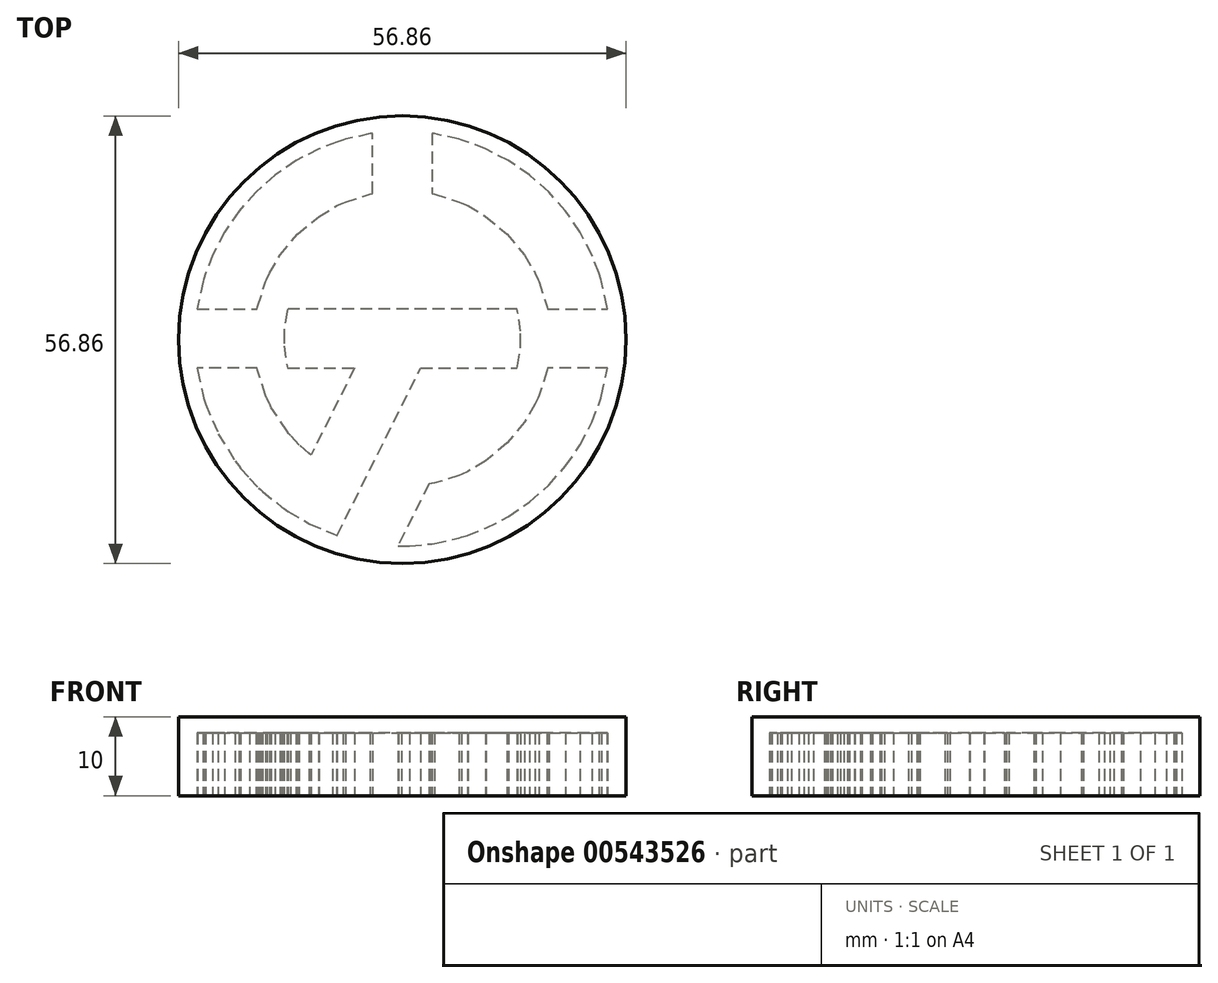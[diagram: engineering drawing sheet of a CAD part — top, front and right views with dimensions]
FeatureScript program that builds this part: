
annotation { "Feature Type Name" : "Feature", "Feature Type Description" : "" }
export const myFeature = defineFeature(function(context is Context, id is Id, definition is map)
    precondition{}
    {
        {
            var Q0;
            Q0=qCreatedBy(makeId("Top.planeOp"),FACE);
            var sketch = newSketch(context, id + "F0", { "sketchPlane" : qUnion([Q0])});
            skLineSegment(sketch, "E0", {"start": v(17.23, -7.39) * mm, "end": v(16.88, -8.2) * mm});
            skLineSegment(sketch, "E1", {"start": v(16.88, -8.2) * mm, "end": v(15.52, -10.46) * mm});
            skLineSegment(sketch, "E2", {"start": v(15.52, -10.46) * mm, "end": v(13.29, -13.15) * mm});
            skLineSegment(sketch, "E3", {"start": v(13.29, -13.15) * mm, "end": v(10.6, -15.39) * mm});
            skLineSegment(sketch, "E4", {"start": v(10.6, -15.39) * mm, "end": v(8.32, -16.75) * mm});
            skLineSegment(sketch, "E5", {"start": v(8.32, -16.75) * mm, "end": v(7.52, -17.1) * mm});
            skLineSegment(sketch, "E6", {"start": v(7.52, -17.1) * mm, "end": v(7.22, -17.23) * mm});
            skLineSegment(sketch, "E7", {"start": v(7.22, -17.23) * mm, "end": v(4.09, -18.23) * mm});
            skLineSegment(sketch, "E8", {"start": v(4.09, -18.23) * mm, "end": v(3.76, -18.3) * mm});
            skLineSegment(sketch, "E9", {"start": v(3.76, -18.3) * mm, "end": v(3.73, -18.3) * mm});
            skLineSegment(sketch, "E10", {"start": v(3.73, -18.3) * mm, "end": v(3.4, -18.36) * mm});
            skLineSegment(sketch, "E11", {"start": v(3.4, -18.36) * mm, "end": v(3.38, -18.36) * mm});
            skLineSegment(sketch, "E12", {"start": v(3.38, -18.36) * mm, "end": v(-0.54, -26.18) * mm});
            skLineSegment(sketch, "E13", {"start": v(-0.54, -26.18) * mm, "end": v(-0.5, -26.19) * mm});
            skLineSegment(sketch, "E14", {"start": v(-0.5, -26.19) * mm, "end": v(-0.12, -26.2) * mm});
            skLineSegment(sketch, "E15", {"start": v(-0.12, -26.2) * mm, "end": v(0, -26.2) * mm});
            skLineSegment(sketch, "E16", {"start": v(0, -26.2) * mm, "end": v(0.94, -26.2) * mm});
            skLineSegment(sketch, "E17", {"start": v(0.94, -26.2) * mm, "end": v(3.45, -25.97) * mm});
            skLineSegment(sketch, "E18", {"start": v(3.45, -25.97) * mm, "end": v(3.76, -25.92) * mm});
            skLineSegment(sketch, "E19", {"start": v(3.76, -25.92) * mm, "end": v(4.08, -25.88) * mm});
            skLineSegment(sketch, "E20", {"start": v(4.08, -25.88) * mm, "end": v(7.22, -25.18) * mm});
            skLineSegment(sketch, "E21", {"start": v(7.22, -25.18) * mm, "end": v(7.52, -25.09) * mm});
            skLineSegment(sketch, "E22", {"start": v(7.52, -25.09) * mm, "end": v(8.3, -24.85) * mm});
            skLineSegment(sketch, "E23", {"start": v(8.3, -24.85) * mm, "end": v(10.61, -23.95) * mm});
            skLineSegment(sketch, "E24", {"start": v(10.61, -23.95) * mm, "end": v(13.51, -22.45) * mm});
            skLineSegment(sketch, "E25", {"start": v(13.51, -22.45) * mm, "end": v(16.18, -20.61) * mm});
            skLineSegment(sketch, "E26", {"start": v(16.18, -20.61) * mm, "end": v(18.6, -18.47) * mm});
            skLineSegment(sketch, "E27", {"start": v(18.6, -18.47) * mm, "end": v(20.75, -16.05) * mm});
            skLineSegment(sketch, "E28", {"start": v(20.75, -16.05) * mm, "end": v(22.58, -13.38) * mm});
            skLineSegment(sketch, "E29", {"start": v(22.58, -13.38) * mm, "end": v(24.08, -10.48) * mm});
            skLineSegment(sketch, "E30", {"start": v(24.08, -10.48) * mm, "end": v(24.99, -8.18) * mm});
            skLineSegment(sketch, "E31", {"start": v(24.99, -8.18) * mm, "end": v(25.22, -7.39) * mm});
            skLineSegment(sketch, "E32", {"start": v(25.22, -7.39) * mm, "end": v(25.31, -7.08) * mm});
            skLineSegment(sketch, "E33", {"start": v(25.31, -7.08) * mm, "end": v(26.01, -3.95) * mm});
            skLineSegment(sketch, "E34", {"start": v(26.01, -3.95) * mm, "end": v(26.06, -3.63) * mm});
            skLineSegment(sketch, "E35", {"start": v(26.06, -3.63) * mm, "end": v(18.43, -3.63) * mm});
            skLineSegment(sketch, "E36", {"start": v(18.43, -3.63) * mm, "end": v(18.36, -3.95) * mm});
            skLineSegment(sketch, "E37", {"start": v(18.36, -3.95) * mm, "end": v(17.36, -7.09) * mm});
            skLineSegment(sketch, "E38", {"start": v(17.36, -7.09) * mm, "end": v(17.23, -7.39) * mm});
            skLineSegment(sketch, "E39", {"start": v(17.23, 7.65) * mm, "end": v(17.36, 7.36) * mm});
            skLineSegment(sketch, "E40", {"start": v(17.36, 7.36) * mm, "end": v(18.36, 4.22) * mm});
            skLineSegment(sketch, "E41", {"start": v(18.36, 4.22) * mm, "end": v(18.43, 3.9) * mm});
            skLineSegment(sketch, "E42", {"start": v(18.43, 3.9) * mm, "end": v(26.06, 3.9) * mm});
            skLineSegment(sketch, "E43", {"start": v(26.06, 3.9) * mm, "end": v(26.01, 4.22) * mm});
            skLineSegment(sketch, "E44", {"start": v(26.01, 4.22) * mm, "end": v(25.31, 7.35) * mm});
            skLineSegment(sketch, "E45", {"start": v(25.31, 7.35) * mm, "end": v(25.22, 7.65) * mm});
            skLineSegment(sketch, "E46", {"start": v(25.22, 7.65) * mm, "end": v(24.99, 8.44) * mm});
            skLineSegment(sketch, "E47", {"start": v(24.99, 8.44) * mm, "end": v(24.08, 10.75) * mm});
            skLineSegment(sketch, "E48", {"start": v(24.08, 10.75) * mm, "end": v(22.58, 13.65) * mm});
            skLineSegment(sketch, "E49", {"start": v(22.58, 13.65) * mm, "end": v(20.75, 16.32) * mm});
            skLineSegment(sketch, "E50", {"start": v(20.75, 16.32) * mm, "end": v(18.6, 18.74) * mm});
            skLineSegment(sketch, "E51", {"start": v(18.6, 18.74) * mm, "end": v(16.18, 20.88) * mm});
            skLineSegment(sketch, "E52", {"start": v(16.18, 20.88) * mm, "end": v(13.51, 22.72) * mm});
            skLineSegment(sketch, "E53", {"start": v(13.51, 22.72) * mm, "end": v(10.61, 24.22) * mm});
            skLineSegment(sketch, "E54", {"start": v(10.61, 24.22) * mm, "end": v(8.3, 25.12) * mm});
            skLineSegment(sketch, "E55", {"start": v(8.3, 25.12) * mm, "end": v(7.52, 25.36) * mm});
            skLineSegment(sketch, "E56", {"start": v(7.52, 25.36) * mm, "end": v(7.22, 25.45) * mm});
            skLineSegment(sketch, "E57", {"start": v(7.22, 25.45) * mm, "end": v(4.08, 26.15) * mm});
            skLineSegment(sketch, "E58", {"start": v(4.08, 26.15) * mm, "end": v(3.76, 26.2) * mm});
            skLineSegment(sketch, "E59", {"start": v(3.76, 26.2) * mm, "end": v(3.76, 18.56) * mm});
            skLineSegment(sketch, "E60", {"start": v(3.76, 18.56) * mm, "end": v(4.09, 18.5) * mm});
            skLineSegment(sketch, "E61", {"start": v(4.09, 18.5) * mm, "end": v(7.22, 17.5) * mm});
            skLineSegment(sketch, "E62", {"start": v(7.22, 17.5) * mm, "end": v(7.52, 17.37) * mm});
            skLineSegment(sketch, "E63", {"start": v(7.52, 17.37) * mm, "end": v(8.32, 17.02) * mm});
            skLineSegment(sketch, "E64", {"start": v(8.32, 17.02) * mm, "end": v(10.6, 15.66) * mm});
            skLineSegment(sketch, "E65", {"start": v(10.6, 15.66) * mm, "end": v(13.29, 13.42) * mm});
            skLineSegment(sketch, "E66", {"start": v(13.29, 13.42) * mm, "end": v(15.52, 10.73) * mm});
            skLineSegment(sketch, "E67", {"start": v(15.52, 10.73) * mm, "end": v(16.88, 8.46) * mm});
            skLineSegment(sketch, "E68", {"start": v(16.88, 8.46) * mm, "end": v(17.23, 7.65) * mm});
            skLineSegment(sketch, "E69", {"start": v(2.33, -3.63) * mm, "end": v(14.57, -3.63) * mm});
            skLineSegment(sketch, "E70", {"start": v(14.57, -3.63) * mm, "end": v(14.64, -3.33) * mm});
            skLineSegment(sketch, "E71", {"start": v(14.64, -3.33) * mm, "end": v(15.04, -0.73) * mm});
            skLineSegment(sketch, "E72", {"start": v(15.04, -0.73) * mm, "end": v(15.04, 0.13) * mm});
            skLineSegment(sketch, "E73", {"start": v(15.04, 0.13) * mm, "end": v(15.04, 1.07) * mm});
            skLineSegment(sketch, "E74", {"start": v(15.04, 1.07) * mm, "end": v(14.64, 3.6) * mm});
            skLineSegment(sketch, "E75", {"start": v(14.64, 3.6) * mm, "end": v(14.57, 3.9) * mm});
            skLineSegment(sketch, "E76", {"start": v(14.57, 3.9) * mm, "end": v(-14.57, 3.9) * mm});
            skLineSegment(sketch, "E77", {"start": v(-14.57, 3.9) * mm, "end": v(-14.64, 3.6) * mm});
            skLineSegment(sketch, "E78", {"start": v(-14.64, 3.6) * mm, "end": v(-15.04, 1) * mm});
            skLineSegment(sketch, "E79", {"start": v(-15.04, 1) * mm, "end": v(-15.04, 0.13) * mm});
            skLineSegment(sketch, "E80", {"start": v(-15.04, 0.13) * mm, "end": v(-15.04, -0.8) * mm});
            skLineSegment(sketch, "E81", {"start": v(-15.04, -0.8) * mm, "end": v(-14.64, -3.33) * mm});
            skLineSegment(sketch, "E82", {"start": v(-14.64, -3.33) * mm, "end": v(-14.57, -3.63) * mm});
            skLineSegment(sketch, "E83", {"start": v(-14.57, -3.63) * mm, "end": v(-6.08, -3.63) * mm});
            skLineSegment(sketch, "E84", {"start": v(-6.08, -3.63) * mm, "end": v(-11.6, -14.65) * mm});
            skLineSegment(sketch, "E85", {"start": v(-11.6, -14.65) * mm, "end": v(-11.86, -14.45) * mm});
            skLineSegment(sketch, "E86", {"start": v(-11.86, -14.45) * mm, "end": v(-13.09, -13.35) * mm});
            skLineSegment(sketch, "E87", {"start": v(-13.09, -13.35) * mm, "end": v(-14.22, -12.16) * mm});
            skLineSegment(sketch, "E88", {"start": v(-14.22, -12.16) * mm, "end": v(-14.43, -11.9) * mm});
            skLineSegment(sketch, "E89", {"start": v(-14.43, -11.9) * mm, "end": v(-14.67, -11.63) * mm});
            skLineSegment(sketch, "E90", {"start": v(-14.67, -11.63) * mm, "end": v(-16.66, -8.6) * mm});
            skLineSegment(sketch, "E91", {"start": v(-16.66, -8.6) * mm, "end": v(-16.82, -8.26) * mm});
            skLineSegment(sketch, "E92", {"start": v(-16.82, -8.26) * mm, "end": v(-16.86, -8.2) * mm});
            skLineSegment(sketch, "E93", {"start": v(-16.86, -8.2) * mm, "end": v(-17.2, -7.46) * mm});
            skLineSegment(sketch, "E94", {"start": v(-17.2, -7.46) * mm, "end": v(-17.23, -7.39) * mm});
            skLineSegment(sketch, "E95", {"start": v(-17.23, -7.39) * mm, "end": v(-17.36, -7.09) * mm});
            skLineSegment(sketch, "E96", {"start": v(-17.36, -7.09) * mm, "end": v(-18.36, -3.95) * mm});
            skLineSegment(sketch, "E97", {"start": v(-18.36, -3.95) * mm, "end": v(-18.43, -3.63) * mm});
            skLineSegment(sketch, "E98", {"start": v(-18.43, -3.63) * mm, "end": v(-26.06, -3.63) * mm});
            skLineSegment(sketch, "E99", {"start": v(-26.06, -3.63) * mm, "end": v(-26.01, -3.95) * mm});
            skLineSegment(sketch, "E100", {"start": v(-26.01, -3.95) * mm, "end": v(-25.32, -7.08) * mm});
            skLineSegment(sketch, "E101", {"start": v(-25.32, -7.08) * mm, "end": v(-25.22, -7.39) * mm});
            skLineSegment(sketch, "E102", {"start": v(-25.22, -7.39) * mm, "end": v(-24.99, -8.19) * mm});
            skLineSegment(sketch, "E103", {"start": v(-24.99, -8.19) * mm, "end": v(-23.37, -11.97) * mm});
            skLineSegment(sketch, "E104", {"start": v(-23.37, -11.97) * mm, "end": v(-21.23, -15.43) * mm});
            skLineSegment(sketch, "E105", {"start": v(-21.23, -15.43) * mm, "end": v(-20.73, -16.07) * mm});
            skLineSegment(sketch, "E106", {"start": v(-20.73, -16.07) * mm, "end": v(-20.52, -16.34) * mm});
            skLineSegment(sketch, "E107", {"start": v(-20.52, -16.34) * mm, "end": v(-19.42, -17.62) * mm});
            skLineSegment(sketch, "E108", {"start": v(-19.42, -17.62) * mm, "end": v(-18.25, -18.82) * mm});
            skLineSegment(sketch, "E109", {"start": v(-18.25, -18.82) * mm, "end": v(-18, -19.05) * mm});
            skLineSegment(sketch, "E110", {"start": v(-18, -19.05) * mm, "end": v(-17.77, -19.27) * mm});
            skLineSegment(sketch, "E111", {"start": v(-17.77, -19.27) * mm, "end": v(-15.27, -21.3) * mm});
            skLineSegment(sketch, "E112", {"start": v(-15.27, -21.3) * mm, "end": v(-15, -21.48) * mm});
            skLineSegment(sketch, "E113", {"start": v(-15, -21.48) * mm, "end": v(-14.5, -21.84) * mm});
            skLineSegment(sketch, "E114", {"start": v(-14.5, -21.84) * mm, "end": v(-11.78, -23.4) * mm});
            skLineSegment(sketch, "E115", {"start": v(-11.78, -23.4) * mm, "end": v(-8.89, -24.65) * mm});
            skLineSegment(sketch, "E116", {"start": v(-8.89, -24.65) * mm, "end": v(-8.28, -24.85) * mm});
            skLineSegment(sketch, "E117", {"start": v(-8.28, -24.85) * mm, "end": v(2.33, -3.63) * mm});
            skLineSegment(sketch, "E118", {"start": v(-17.23, 7.65) * mm, "end": v(-16.88, 8.46) * mm});
            skLineSegment(sketch, "E119", {"start": v(-16.88, 8.46) * mm, "end": v(-15.52, 10.73) * mm});
            skLineSegment(sketch, "E120", {"start": v(-15.52, 10.73) * mm, "end": v(-13.29, 13.42) * mm});
            skLineSegment(sketch, "E121", {"start": v(-13.29, 13.42) * mm, "end": v(-10.6, 15.66) * mm});
            skLineSegment(sketch, "E122", {"start": v(-10.6, 15.66) * mm, "end": v(-8.32, 17.02) * mm});
            skLineSegment(sketch, "E123", {"start": v(-8.32, 17.02) * mm, "end": v(-7.52, 17.37) * mm});
            skLineSegment(sketch, "E124", {"start": v(-7.52, 17.37) * mm, "end": v(-7.22, 17.5) * mm});
            skLineSegment(sketch, "E125", {"start": v(-7.22, 17.5) * mm, "end": v(-4.09, 18.5) * mm});
            skLineSegment(sketch, "E126", {"start": v(-4.09, 18.5) * mm, "end": v(-3.76, 18.56) * mm});
            skLineSegment(sketch, "E127", {"start": v(-3.76, 18.56) * mm, "end": v(-3.76, 26.2) * mm});
            skLineSegment(sketch, "E128", {"start": v(-3.76, 26.2) * mm, "end": v(-4.08, 26.15) * mm});
            skLineSegment(sketch, "E129", {"start": v(-4.08, 26.15) * mm, "end": v(-7.22, 25.45) * mm});
            skLineSegment(sketch, "E130", {"start": v(-7.22, 25.45) * mm, "end": v(-7.52, 25.36) * mm});
            skLineSegment(sketch, "E131", {"start": v(-7.52, 25.36) * mm, "end": v(-8.31, 25.12) * mm});
            skLineSegment(sketch, "E132", {"start": v(-8.31, 25.12) * mm, "end": v(-10.61, 24.22) * mm});
            skLineSegment(sketch, "E133", {"start": v(-10.61, 24.22) * mm, "end": v(-13.51, 22.72) * mm});
            skLineSegment(sketch, "E134", {"start": v(-13.51, 22.72) * mm, "end": v(-16.18, 20.88) * mm});
            skLineSegment(sketch, "E135", {"start": v(-16.18, 20.88) * mm, "end": v(-18.6, 18.74) * mm});
            skLineSegment(sketch, "E136", {"start": v(-18.6, 18.74) * mm, "end": v(-20.75, 16.32) * mm});
            skLineSegment(sketch, "E137", {"start": v(-20.75, 16.32) * mm, "end": v(-22.58, 13.65) * mm});
            skLineSegment(sketch, "E138", {"start": v(-22.58, 13.65) * mm, "end": v(-24.09, 10.75) * mm});
            skLineSegment(sketch, "E139", {"start": v(-24.09, 10.75) * mm, "end": v(-24.99, 8.44) * mm});
            skLineSegment(sketch, "E140", {"start": v(-24.99, 8.44) * mm, "end": v(-25.22, 7.65) * mm});
            skLineSegment(sketch, "E141", {"start": v(-25.22, 7.65) * mm, "end": v(-25.32, 7.35) * mm});
            skLineSegment(sketch, "E142", {"start": v(-25.32, 7.35) * mm, "end": v(-26.01, 4.22) * mm});
            skLineSegment(sketch, "E143", {"start": v(-26.01, 4.22) * mm, "end": v(-26.06, 3.9) * mm});
            skLineSegment(sketch, "E144", {"start": v(-26.06, 3.9) * mm, "end": v(-18.43, 3.9) * mm});
            skLineSegment(sketch, "E145", {"start": v(-18.43, 3.9) * mm, "end": v(-18.36, 4.22) * mm});
            skLineSegment(sketch, "E146", {"start": v(-18.36, 4.22) * mm, "end": v(-17.36, 7.36) * mm});
            skLineSegment(sketch, "E147", {"start": v(-17.36, 7.36) * mm, "end": v(-17.23, 7.65) * mm});
            skSolve(sketch);
        }
        {
            var Q0;
            Q0=qCreatedBy(makeId("Top.planeOp"),FACE);
            var sketch = newSketch(context, id + "F1", { "sketchPlane" : qUnion([Q0])});
            skCircle(sketch, "E148", {"center": v(0, 0) * mm, "radius": 28.43 * mm});
            skSolve(sketch);
        }
        {
            var Q0;
            Q0 = qSketchRegion(id + "F1", true);
            extrude(context, id + "F2", {"entities" : qUnion([Q0]), "depth" : 10 * mm, "offsetDistance" : 25 * mm});
        }
        {
            var Q0;
            Q0=makeQuery(id+"F0.imprint","IMPRINT",FACE,{"disambiguationData":[TD([[makeQuery(id+"F0.imprint","IMPRINT",EDGE,{"derivedFrom":sQuery(id+"F0.wireOp",EDGE,"E118")}),1.0]])]});
            var Q1;
            Q1=makeQuery(id+"F0.imprint","IMPRINT",FACE,{"disambiguationData":[TD([[makeQuery(id+"F0.imprint","IMPRINT",EDGE,{"derivedFrom":sQuery(id+"F0.wireOp",EDGE,"E39")}),1.0]])]});
            var Q2;
            Q2=makeQuery(id+"F0.imprint","IMPRINT",FACE,{"disambiguationData":[TD([[makeQuery(id+"F0.imprint","IMPRINT",EDGE,{"derivedFrom":sQuery(id+"F0.wireOp",EDGE,"E69")}),1.0]])]});
            var Q3;
            Q3=makeQuery(id+"F0.imprint","IMPRINT",FACE,{"disambiguationData":[TD([[makeQuery(id+"F0.imprint","IMPRINT",EDGE,{"derivedFrom":sQuery(id+"F0.wireOp",EDGE,"E0")}),1.0]])]});
            extrude(context, id + "F3", {"entities" : qUnion([Q0, Q1, Q2, Q3]), "operationType" : NewBodyOperationType.REMOVE, "depth" : 8 * mm, "offsetDistance" : 25 * mm});
        }
    });
